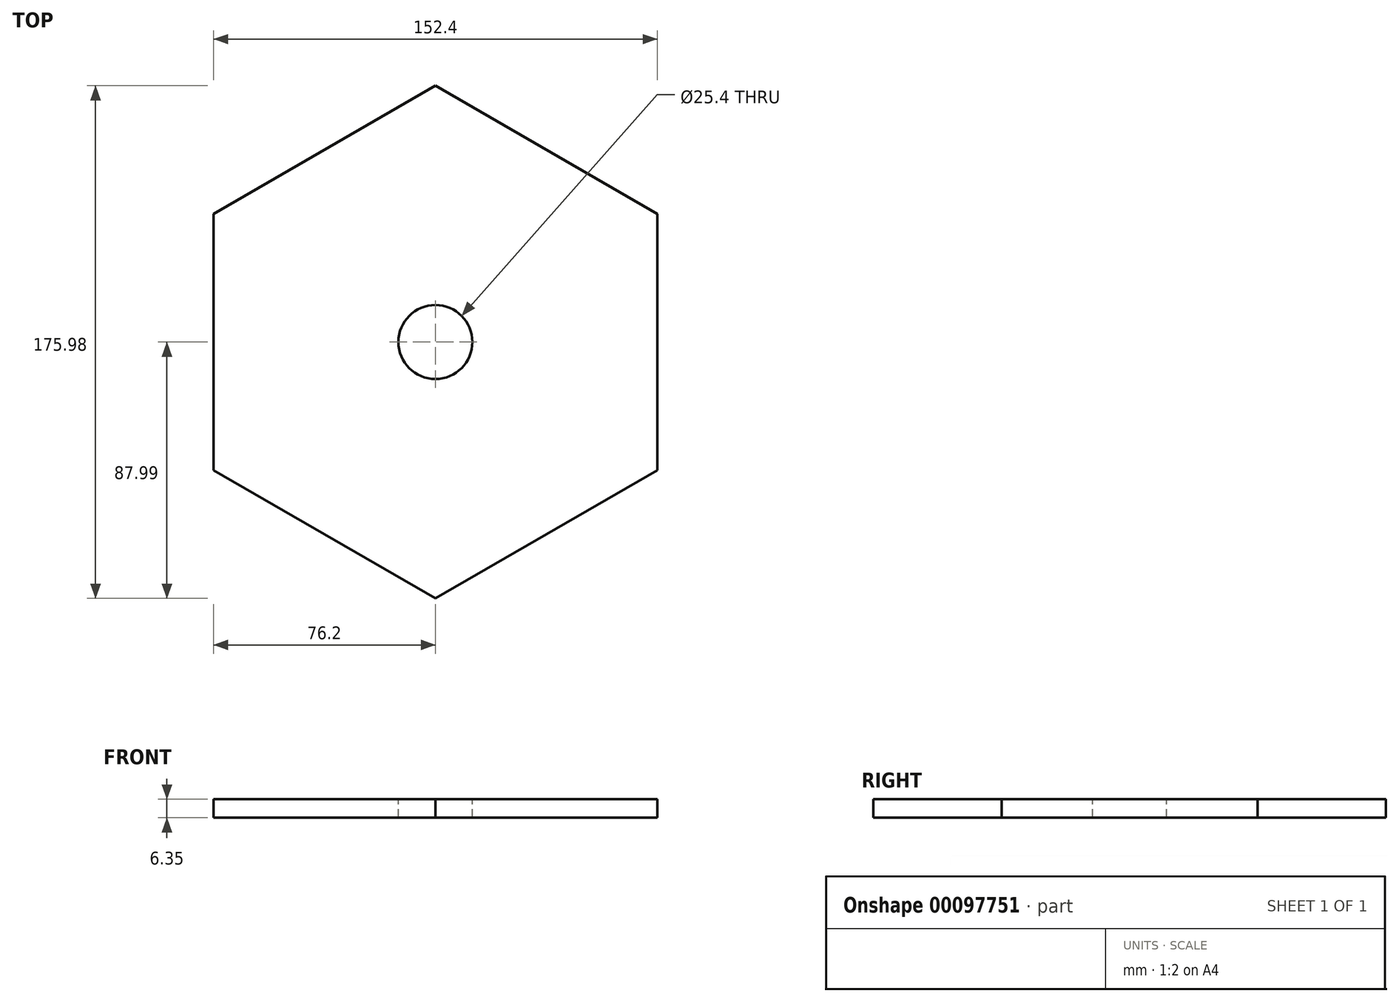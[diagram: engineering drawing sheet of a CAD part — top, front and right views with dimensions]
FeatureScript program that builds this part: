
annotation { "Feature Type Name" : "Feature", "Feature Type Description" : "" }
export const myFeature = defineFeature(function(context is Context, id is Id, definition is map)
    precondition{}
    {
        {
            var Q0;
            Q0=qCreatedBy(makeId("Top.planeOp"),FACE);
            var sketch = newSketch(context, id + "F0", { "sketchPlane" : qUnion([Q0])});
            skCircle(sketch, "E0.cCircle", {"center": v(0, 0) * mm, "radius": 76.2 * mm, "construction": true});
            skLineSegment(sketch, "E0.0", {"start": v(76.2, -44) * mm, "end": v(0, -87.99) * mm});
            skLineSegment(sketch, "E0.1", {"start": v(0, -87.99) * mm, "end": v(-76.2, -44) * mm});
            skLineSegment(sketch, "E0.2", {"start": v(-76.2, -44) * mm, "end": v(-76.2, 44) * mm});
            skLineSegment(sketch, "E0.3", {"start": v(-76.2, 44) * mm, "end": v(0, 87.99) * mm});
            skLineSegment(sketch, "E0.4", {"start": v(0, 87.99) * mm, "end": v(76.2, 44) * mm});
            skLineSegment(sketch, "E0.5", {"start": v(76.2, 44) * mm, "end": v(76.2, -44) * mm});
            skPoint(sketch, "E0.0.midPoint", {"position": v(38.1, -66) * mm});
            skLineSegment(sketch, "E1", {"start": v(0, 87.99) * mm, "end": v(0, -87.99) * mm, "construction": true});
            skSolve(sketch);
        }
        {
            var Q0;
            Q0 = qSketchRegion(id + "F0", true);
            extrude(context, id + "F1", {"entities" : qUnion([Q0]), "depth" : 6.35 * mm});
        }
        {
            var Q0;
            Q0=makeQuery(id+"F1.opExtrude","CAP_FACE",FACE,{"disambiguationData":[OSD([sQuery(id+"F0.wireOp",EDGE,"E0.0"),sQuery(id+"F0.wireOp",EDGE,"E0.1"),sQuery(id+"F0.wireOp",EDGE,"E0.2"),sQuery(id+"F0.wireOp",EDGE,"E0.3"),sQuery(id+"F0.wireOp",EDGE,"E0.4"),sQuery(id+"F0.wireOp",EDGE,"E0.5")])],"isStart":false});
            var sketch = newSketch(context, id + "F2", { "sketchPlane" : qUnion([Q0])});
            skCircle(sketch, "E2", {"center": v(0, 0) * mm, "radius": 12.7 * mm});
            skSolve(sketch);
        }
        {
            var Q0;
            Q0 = qSketchRegion(id + "F2", true);
            extrude(context, id + "F3", {"entities" : qUnion([Q0]), "operationType" : NewBodyOperationType.REMOVE, "oppositeDirection" : true, "depth" : 25.4 * mm});
        }
    });
